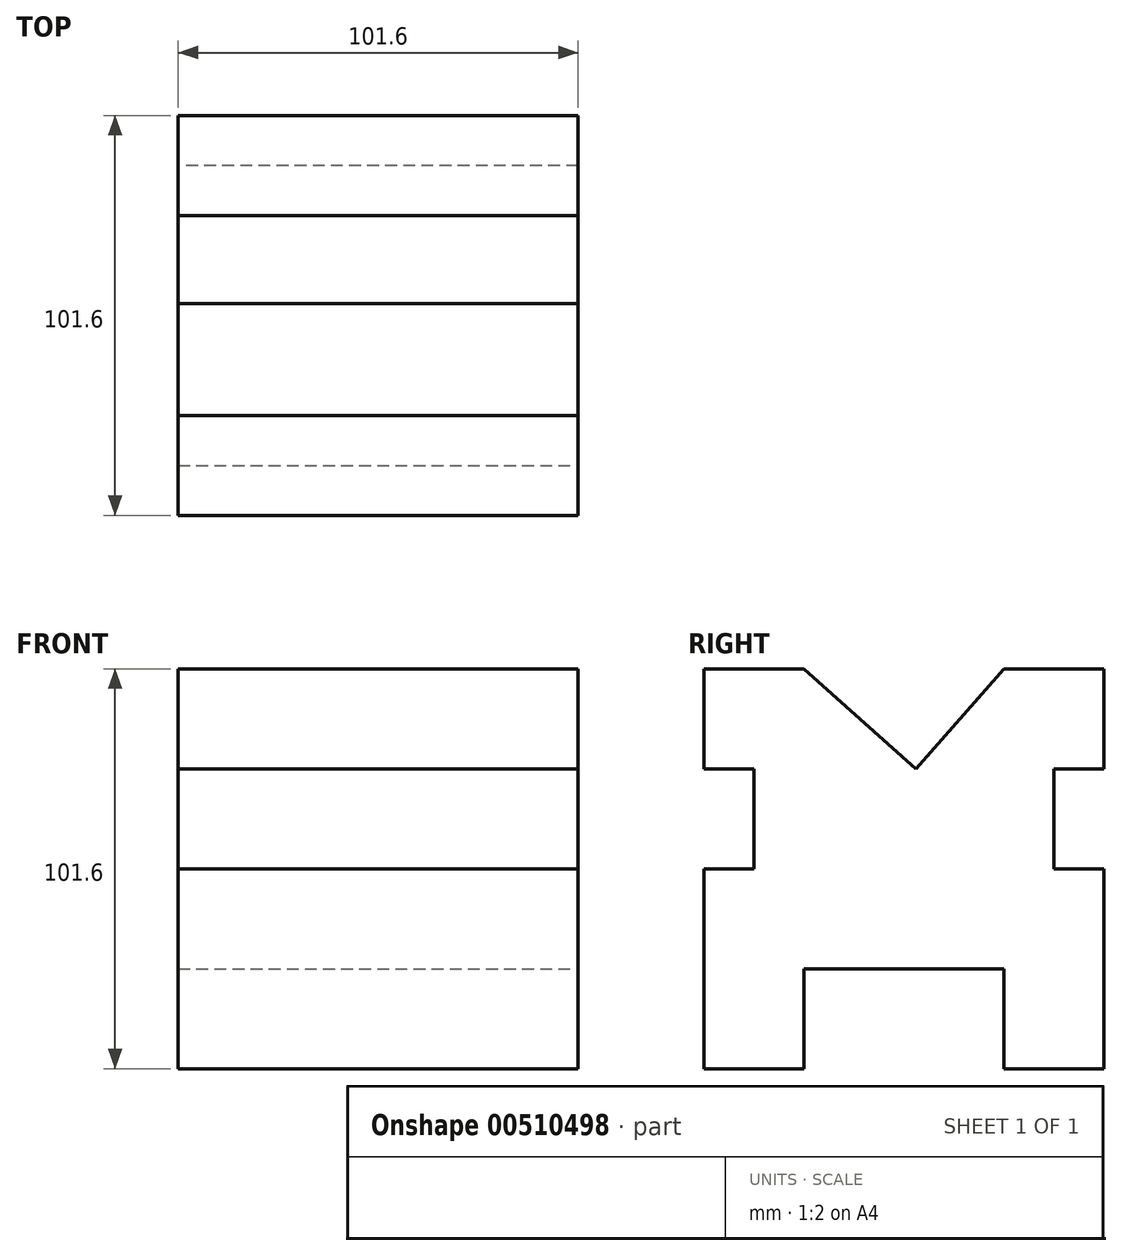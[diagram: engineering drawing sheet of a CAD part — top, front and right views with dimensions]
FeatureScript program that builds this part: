
annotation { "Feature Type Name" : "Feature", "Feature Type Description" : "" }
export const myFeature = defineFeature(function(context is Context, id is Id, definition is map)
    precondition{}
    {
        {
            var Q0;
            Q0=qCreatedBy(makeId("Front.planeOp"),FACE);
            var sketch = newSketch(context, id + "F0", { "sketchPlane" : qUnion([Q0])});
            skLineSegment(sketch, "E0.bottom", {"start": v(0, 0) * mm, "end": v(-101.6, 0) * mm});
            skLineSegment(sketch, "E0.top", {"start": v(0, 101.6) * mm, "end": v(-101.6, 101.6) * mm});
            skLineSegment(sketch, "E0.left", {"start": v(0, 0) * mm, "end": v(0, 101.6) * mm});
            skLineSegment(sketch, "E0.right", {"start": v(-101.6, 0) * mm, "end": v(-101.6, 101.6) * mm});
            skSolve(sketch);
        }
        {
            var Q0;
            Q0=makeQuery(id+"F0.imprint","IMPRINT",FACE,{"disambiguationData":[TD([[makeQuery(id+"F0.imprint","IMPRINT",EDGE,{"derivedFrom":sQuery(id+"F0.wireOp",EDGE,"E0.bottom")}),-1.0]])]});
            extrude(context, id + "F1", {"entities" : qUnion([Q0]), "depth" : 101.6 * mm});
        }
        {
            var Q0;
            Q0=makeQuery(id+"F1.opExtrude","SWEPT_FACE",FACE,{"disambiguationData":[OSD([sQuery(id+"F0.wireOp",EDGE,"E0.left")])]});
            var sketch = newSketch(context, id + "F2", { "sketchPlane" : qUnion([Q0])});
            skLineSegment(sketch, "E1", {"start": v(-101.6, 0) * mm, "end": v(-101.6, 50.8) * mm});
            skLineSegment(sketch, "E2", {"start": v(-101.6, 50.8) * mm, "end": v(-88.9, 50.8) * mm});
            skLineSegment(sketch, "E3", {"start": v(-88.9, 50.8) * mm, "end": v(-88.9, 76.2) * mm});
            skLineSegment(sketch, "E4", {"start": v(-88.9, 76.2) * mm, "end": v(-101.6, 76.2) * mm});
            skSolve(sketch);
        }
        {
            var Q0;
            {var subQ0=sQuery(id+"F2.wireOp",EDGE,"E2");Q0=makeQuery(id+"F2.imprint","IMPRINT",FACE,{"disambiguationData":[TD([[makeQuery(id+"F2.imprint","IMPRINT",EDGE,{"derivedFrom":subQ0}),1.0]])]});}
            extrude(context, id + "F3", {"entities" : qUnion([Q0]), "operationType" : NewBodyOperationType.REMOVE, "oppositeDirection" : true, "depth" : 101.6 * mm});
        }
        {
            var Q0;
            Q0=makeQuery(id+"F1.opExtrude","SWEPT_FACE",FACE,{"disambiguationData":[OSD([sQuery(id+"F0.wireOp",EDGE,"E0.left")])]});
            var sketch = newSketch(context, id + "F4", { "sketchPlane" : qUnion([Q0])});
            skLineSegment(sketch, "E5", {"start": v(-101.6, 0) * mm, "end": v(-76.2, 0) * mm});
            skLineSegment(sketch, "E6", {"start": v(-76.2, 0) * mm, "end": v(-76.2, 25.4) * mm});
            skLineSegment(sketch, "E7", {"start": v(-76.2, 25.4) * mm, "end": v(-25.4, 25.4) * mm});
            skLineSegment(sketch, "E8", {"start": v(-25.4, 25.4) * mm, "end": v(-25.4, 0) * mm});
            skSolve(sketch);
        }
        {
            var Q0;
            {var subQ0=sQuery(id+"F4.wireOp",EDGE,"E6");Q0=makeQuery(id+"F4.imprint","IMPRINT",FACE,{"disambiguationData":[TD([[makeQuery(id+"F4.imprint","IMPRINT",EDGE,{"derivedFrom":subQ0}),-1.0]])]});}
            extrude(context, id + "F5", {"entities" : qUnion([Q0]), "operationType" : NewBodyOperationType.REMOVE, "oppositeDirection" : true, "depth" : 127 * mm});
        }
        {
            var Q0;
            Q0=makeQuery(id+"F1.opExtrude","SWEPT_FACE",FACE,{"disambiguationData":[OSD([sQuery(id+"F0.wireOp",EDGE,"E0.right")])]});
            var sketch = newSketch(context, id + "F6", { "sketchPlane" : qUnion([Q0])});
            skLineSegment(sketch, "E9", {"start": v(88.9, 50.8) * mm, "end": v(0, 50.8) * mm});
            skLineSegment(sketch, "E10", {"start": v(0, 50.8) * mm, "end": v(0, 76.2) * mm});
            skLineSegment(sketch, "E11", {"start": v(0, 76.2) * mm, "end": v(12.7, 76.2) * mm});
            skLineSegment(sketch, "E12", {"start": v(12.7, 76.2) * mm, "end": v(12.7, 50.8) * mm});
            skSolve(sketch);
        }
        {
            var Q0;
            {var subQ0=sQuery(id+"F6.wireOp",EDGE,"E10");Q0=makeQuery(id+"F6.imprint","IMPRINT",FACE,{"disambiguationData":[TD([[makeQuery(id+"F6.imprint","IMPRINT",EDGE,{"derivedFrom":subQ0}),-1.0]])]});}
            extrude(context, id + "F7", {"entities" : qUnion([Q0]), "operationType" : NewBodyOperationType.REMOVE, "oppositeDirection" : true, "depth" : 101.6 * mm});
        }
        {
            var Q0;
            Q0=makeQuery(id+"F1.opExtrude","SWEPT_FACE",FACE,{"disambiguationData":[OSD([sQuery(id+"F0.wireOp",EDGE,"E0.left")])]});
            var sketch = newSketch(context, id + "F8", { "sketchPlane" : qUnion([Q0])});
            skLineSegment(sketch, "E13", {"start": v(-101.6, 101.6) * mm, "end": v(-76.2, 101.6) * mm});
            skLineSegment(sketch, "E14", {"start": v(-47.8, 76.2) * mm, "end": v(-19.4, 101.6) * mm});
            skLineSegment(sketch, "E15", {"start": v(-19.4, 101.6) * mm, "end": v(0, 101.6) * mm});
            skLineSegment(sketch, "E16", {"start": v(0, 101.6) * mm, "end": v(-25.4, 101.6) * mm});
            skLineSegment(sketch, "E17", {"start": v(-25.4, 101.6) * mm, "end": v(-47.8, 76.2) * mm});
            skLineSegment(sketch, "E18", {"start": v(-47.8, 76.2) * mm, "end": v(-76.2, 101.6) * mm});
            skSolve(sketch);
        }
        {
            var Q0;
            {var subQ0=sQuery(id+"F8.wireOp",EDGE,"E17");Q0=makeQuery(id+"F8.imprint","IMPRINT",FACE,{"disambiguationData":[TD([[makeQuery(id+"F8.imprint","IMPRINT",EDGE,{"derivedFrom":subQ0}),-1.0]])]});}
            extrude(context, id + "F9", {"entities" : qUnion([Q0]), "operationType" : NewBodyOperationType.REMOVE, "oppositeDirection" : true, "depth" : 1397 * mm});
        }
    });
